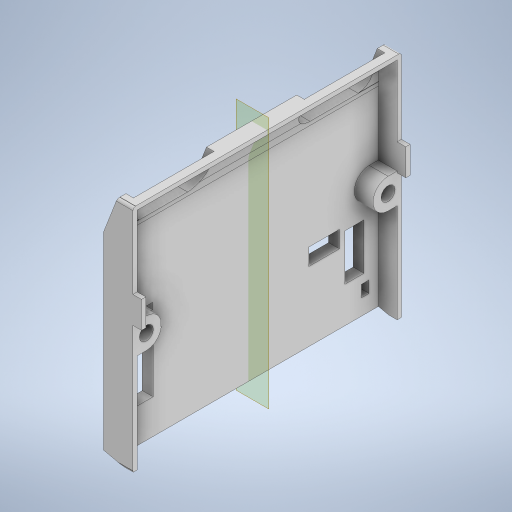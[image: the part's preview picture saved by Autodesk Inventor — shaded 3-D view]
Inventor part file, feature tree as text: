
AUTODESK INVENTOR PART (.ipt)
format: ipt  version: 2023.5 (Build 275446000, 446)  size: 583,680 bytes
history: native  units: mm
features: extrude x16, sketch x15, projected_geometry x13, reference x12, other x5, fillet x2, mirror x1
ambient origin geometry x8: Origin, YZ Plane, XZ Plane, XY Plane, X Axis, Y Axis, Z Axis, Center Point
bodies: Body1 (feature_tree)
feature tree (64):
  other  "Bryła1"
  extrude  "Wyciągnięcie proste1"  Depth=4.0mm TaperAngle=0.0deg
  sketch  "Szkic2"
  extrude  "Wyciągnięcie proste2"  TaperAngle=0.0deg  [1 undecoded]
  extrude  "Wyciągnięcie proste3"  Depth=10.0mm TaperAngle=0.0deg
  extrude  "Wyciągnięcie proste5"  Depth=0.8mm
  extrude  "Wyciągnięcie proste6"  Depth=1.5mm
  extrude  "Wyciągnięcie proste9"  Depth=1.5mm
  extrude  "Wyciągnięcie proste10"  Depth=2.0mm TaperAngle=0.0deg
  extrude  "Wyciągnięcie proste11"  Depth=1.5mm TaperAngle=0.0deg
  extrude  "Wyciągnięcie proste12"  Depth=15.0mm
  other  "Płaszczyzna konstrukcyjna1"
  mirror  "Odbij1"
  extrude  "Wyciągnięcie proste13"  Depth=15.0mm
  extrude  "Wyciągnięcie proste14"  Depth=1.6mm
  extrude  "Wyciągnięcie proste15"  Depth=1.6mm
  extrude  "Wyciągnięcie proste16"  Depth=6.0mm
  extrude  "Wyciągnięcie proste17"  Depth=4.0mm TaperAngle=0.0deg
  extrude  "Wyciągnięcie proste18"  Depth=4.0mm TaperAngle=0.0deg
  extrude  "Wyciągnięcie proste19"  Depth=1.6mm
  fillet  "Zaokrąglenie2"  Radius=10.0mm
  fillet  "Zaokrąglenie3"  Radius=1.0mm
  sketch  "Szkic1"
  projected_geometry  "Pętla rzutowana1"
  sketch  "Szkic4"
  projected_geometry  "Pętla rzutowana4"
  sketch  "Szkic5"
  projected_geometry  "Pętla rzutowana5"
  sketch  "Szkic9"
  projected_geometry  "Pętla rzutowana10"
  sketch  "Szkic10"
  projected_geometry  "Pętla rzutowana11"
  sketch  "Szkic11"
  projected_geometry  "Pętla rzutowana12"
  projected_geometry  "Pętla rzutowana13"
  sketch  "Szkic12"
  projected_geometry  "Pętla rzutowana14"
  sketch  "Szkic13"
  projected_geometry  "Pętla rzutowana15"
  projected_geometry  "Pętla rzutowana16"
  projected_geometry  "Pętla rzutowana17"
  sketch  "Szkic14"
  reference  "Odniesienie4"
  reference  "Odniesienie5"
  reference  "Odniesienie6"
  reference  "Odniesienie7"
  sketch  "Szkic15"
  sketch  "Szkic16"
  sketch  "Szkic17"
  projected_geometry  "Pętla rzutowana18"
  sketch  "Szkic18"
  reference  "Odniesienie8"
  reference  "Odniesienie9"
  reference  "Odniesienie10"
  reference  "Odniesienie11"
  sketch  "Szkic19"
  reference  "Odniesienie12"
  reference  "Odniesienie13"
  projected_geometry  "Pętla rzutowana19"
  reference  "Odniesienie14"
  reference  "Odniesienie15"
  parser-record x1  (decoder bookkeeping rows leaked as tree rows — omitted from the tree; the rows remain in map.json)
  other  "stratos_v2_mechanics.iam"
  other  "MikroSumo:1"
note: 1 required parameter value undecoded (feature->parameter linkage not recoverable at this tier; creation-order binding heuristic only, values carry confidence <= 0.55)
note: 1 file-system path scrubbed to <path> (originals preserved in map.json)
